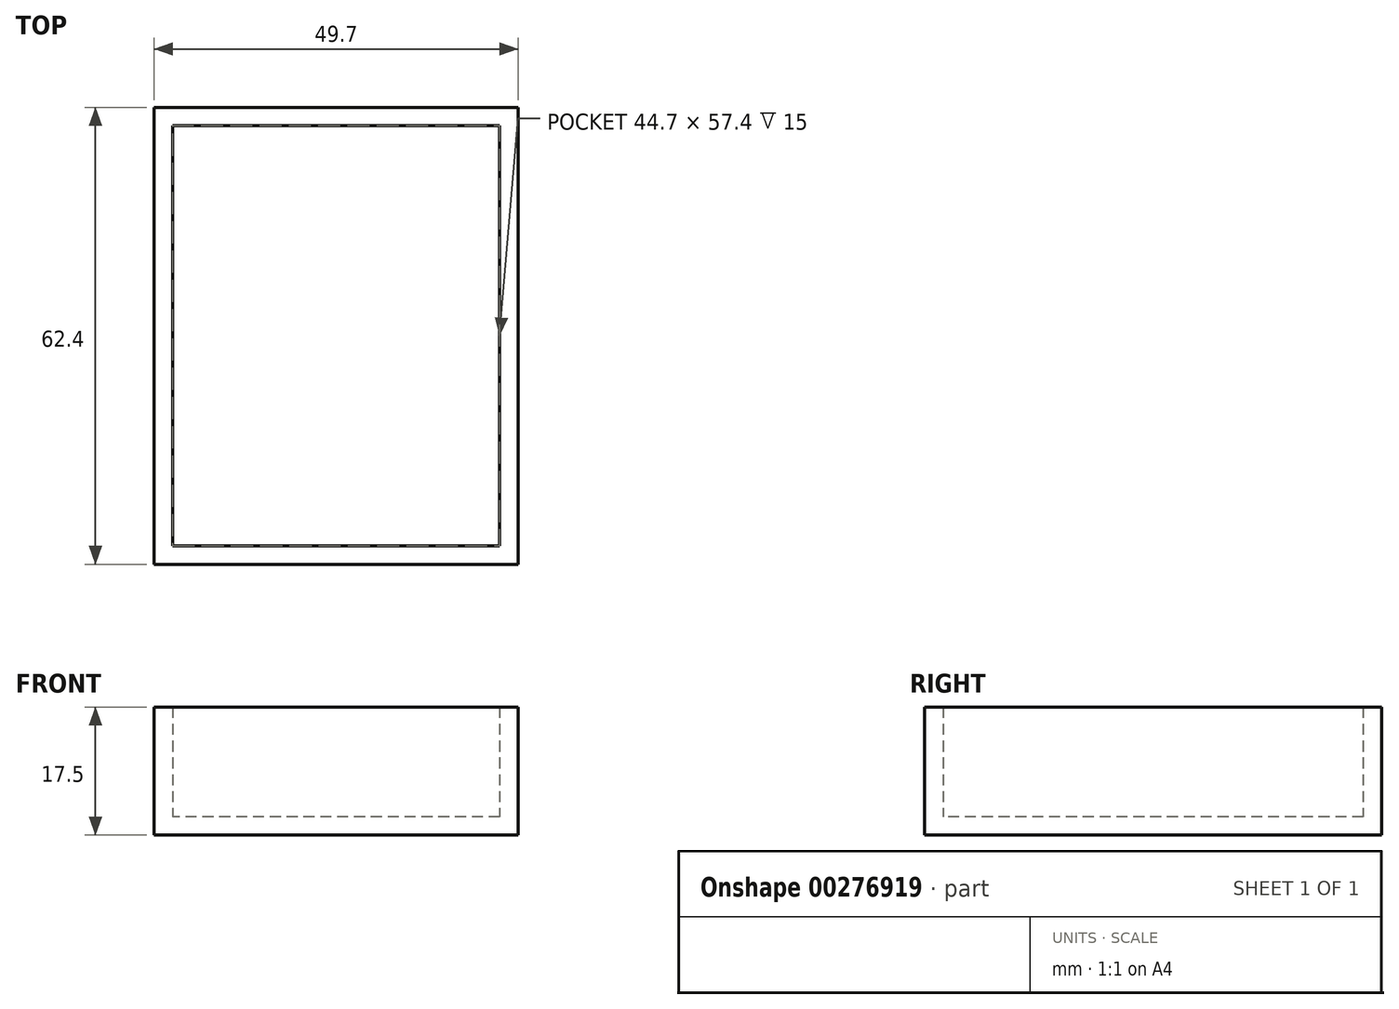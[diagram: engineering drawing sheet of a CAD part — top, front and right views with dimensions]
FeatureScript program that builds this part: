
annotation { "Feature Type Name" : "Feature", "Feature Type Description" : "" }
export const myFeature = defineFeature(function(context is Context, id is Id, definition is map)
    precondition{}
    {
        {
            var Q0;
            Q0=qCreatedBy(makeId("Top.planeOp"),FACE);
            var sketch = newSketch(context, id + "F0", { "sketchPlane" : qUnion([Q0])});
            skLineSegment(sketch, "E0.bottom", {"start": v(22.35, 28.7) * mm, "end": v(-22.35, 28.7) * mm});
            skLineSegment(sketch, "E0.top", {"start": v(22.35, -28.7) * mm, "end": v(-22.35, -28.7) * mm});
            skLineSegment(sketch, "E0.left", {"start": v(22.35, 28.7) * mm, "end": v(22.35, -28.7) * mm});
            skLineSegment(sketch, "E0.right", {"start": v(-22.35, 28.7) * mm, "end": v(-22.35, -28.7) * mm});
            skPoint(sketch, "E0.middle", {"position": v(0, 0) * mm});
            skSolve(sketch);
        }
        {
            var Q0;
            Q0=qSketchRegion(id+"F0",true);
            extrude(context, id + "F1", {"entities" : qUnion([Q0]), "depth" : 15 * mm});
        }
        {
            var Q0;
            Q0=makeQuery(id+"F1.opExtrude","CAP_FACE",FACE,{"disambiguationData":[OSD([sQuery(id+"F0.wireOp",EDGE,"E0.bottom"),sQuery(id+"F0.wireOp",EDGE,"E0.top"),sQuery(id+"F0.wireOp",EDGE,"E0.left"),sQuery(id+"F0.wireOp",EDGE,"E0.right")])],"isStart":false});
            shell(context, id + "F2", {"entities" : qUnion([Q0]), "thickness" : 2.5 * mm, "oppositeDirection" : true});
        }
    });
